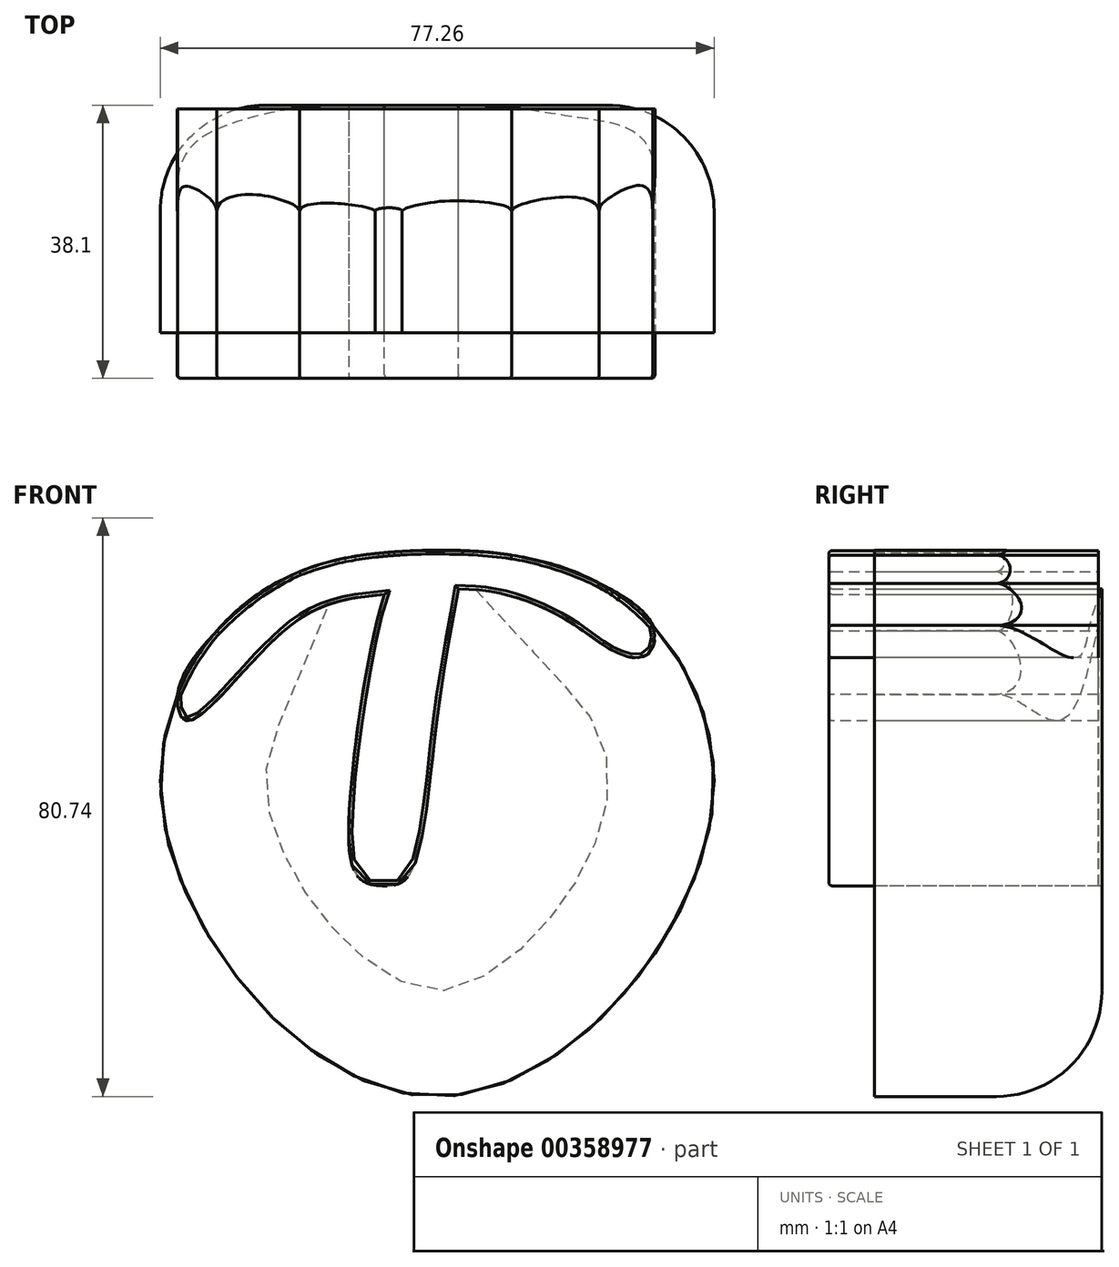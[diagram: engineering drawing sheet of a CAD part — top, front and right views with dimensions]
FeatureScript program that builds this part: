
annotation { "Feature Type Name" : "Feature", "Feature Type Description" : "" }
export const myFeature = defineFeature(function(context is Context, id is Id, definition is map)
    precondition{}
    {
        {
            var Q0;
            Q0=qCreatedBy(makeId("Front.planeOp"),FACE);
            var sketch = newSketch(context, id + "F0", { "sketchPlane" : qUnion([Q0])});
            skFitSpline(sketch, "E0", {"points": [v(0, 38.1) * mm, v(-25.4, 31.75) * mm, v(-38.1, 0) * mm, v(0, -38.1) * mm, v(38.1, 0) * mm, v(25.4, 31.75) * mm, v(0, 38.1) * mm]});
            skFitSpline(sketch, "E1", {"points": [v(-36.21, 18.03) * mm, v(-34.8, 14.34) * mm, v(-20.58, 27.57) * mm, v(-7.35, 31.98) * mm, v(6.86, 32.47) * mm, v(18.62, 28.06) * mm, v(25.49, 23.65) * mm, v(29.4, 23.65) * mm, v(30.05, 27.64) * mm, v(22.58, 33.53) * mm, v(10.37, 37.45) * mm, v(-4.9, 37.98) * mm, v(-19.19, 35.14) * mm, v(-30.73, 26.88) * mm, v(-36.21, 18.03) * mm]});
            skFitSpline(sketch, "E2", {"points": [v(-7.35, 31.98) * mm, v(-12.25, 2.08) * mm, v(-10.78, -7.72) * mm, v(-7.35, -8.7) * mm, v(-3.92, -7.23) * mm, v(0, 14.83) * mm, v(2.95, 32.74) * mm, v(2.45, 34.92) * mm, v(-4.41, 34.92) * mm, v(-7.35, 31.98) * mm]});
            skSolve(sketch);
        }
        {
            var Q0;
            {var subQ0=sQuery(id+"F0.wireOp",EDGE,"E1");var subQ1=sQuery(id+"F0.wireOp",EDGE,"E0");var subQ2=makeQuery(id+"F0.imprint","INTERSECT",VERTEX,{"disambiguationData":[OD(0.0)],"derivedFrom":[subQ1,subQ0]});Q0=makeQuery(id+"F0.imprint","IMPRINT",FACE,{"disambiguationData":[TD([[makeQuery(id+"F0.imprint","IMPRINT",EDGE,{"disambiguationData":[TD([[subQ2,1.0]])],"derivedFrom":subQ1}),1.0]])]});}
            var Q1;
            {var subQ0=sQuery(id+"F0.wireOp",EDGE,"E1");var subQ1=sQuery(id+"F0.wireOp",EDGE,"E0");var subQ2=makeQuery(id+"F0.imprint","INTERSECT",VERTEX,{"disambiguationData":[OD(0.0)],"derivedFrom":[subQ1,subQ0]});Q1=makeQuery(id+"F0.imprint","IMPRINT",FACE,{"disambiguationData":[TD([[makeQuery(id+"F0.imprint","IMPRINT",EDGE,{"disambiguationData":[TD([[subQ2,-1.0]])],"derivedFrom":subQ1}),-1.0]])]});}
            var Q2;
            {var subQ0=sQuery(id+"F0.wireOp",EDGE,"E1");var subQ1=sQuery(id+"F0.wireOp",EDGE,"E0");var subQ2=makeQuery(id+"F0.imprint","INTERSECT",VERTEX,{"disambiguationData":[OD(2.0)],"derivedFrom":[subQ1,subQ0]});Q2=makeQuery(id+"F0.imprint","IMPRINT",FACE,{"disambiguationData":[TD([[makeQuery(id+"F0.imprint","IMPRINT",EDGE,{"disambiguationData":[TD([[subQ2,-1.0]])],"derivedFrom":subQ1}),1.0]])]});}
            var Q3;
            {var subQ0=sQuery(id+"F0.wireOp",EDGE,"E1");var subQ1=sQuery(id+"F0.wireOp",EDGE,"E0");var subQ2=makeQuery(id+"F0.imprint","INTERSECT",VERTEX,{"disambiguationData":[OD(3.0)],"derivedFrom":[subQ1,subQ0]});Q3=makeQuery(id+"F0.imprint","IMPRINT",FACE,{"disambiguationData":[TD([[makeQuery(id+"F0.imprint","IMPRINT",EDGE,{"disambiguationData":[TD([[subQ2,-1.0]])],"derivedFrom":subQ1}),-1.0]])]});}
            var Q4;
            {var subQ0=sQuery(id+"F0.wireOp",EDGE,"E1");var subQ1=sQuery(id+"F0.wireOp",EDGE,"E0");var subQ2=makeQuery(id+"F0.imprint","INTERSECT",VERTEX,{"disambiguationData":[OD(5.0)],"derivedFrom":[subQ1,subQ0]});Q4=makeQuery(id+"F0.imprint","IMPRINT",FACE,{"disambiguationData":[TD([[makeQuery(id+"F0.imprint","IMPRINT",EDGE,{"disambiguationData":[TD([[subQ2,-1.0]])],"derivedFrom":subQ1}),-1.0]])]});}
            var Q5;
            {var subQ0=sQuery(id+"F0.wireOp",EDGE,"E1");var subQ1=sQuery(id+"F0.wireOp",EDGE,"E0");var subQ2=makeQuery(id+"F0.imprint","INTERSECT",VERTEX,{"disambiguationData":[OD(6.0)],"derivedFrom":[subQ1,subQ0]});Q5=makeQuery(id+"F0.imprint","IMPRINT",FACE,{"disambiguationData":[TD([[makeQuery(id+"F0.imprint","IMPRINT",EDGE,{"disambiguationData":[TD([[subQ2,-1.0]])],"derivedFrom":subQ1}),1.0]])]});}
            var Q6;
            {var subQ0=sQuery(id+"F0.wireOp",EDGE,"E1");var subQ1=sQuery(id+"F0.wireOp",EDGE,"E0");var subQ2=makeQuery(id+"F0.imprint","INTERSECT",VERTEX,{"disambiguationData":[OD(1.0)],"derivedFrom":[subQ1,subQ0]});Q6=makeQuery(id+"F0.imprint","IMPRINT",FACE,{"disambiguationData":[TD([[makeQuery(id+"F0.imprint","IMPRINT",EDGE,{"disambiguationData":[TD([[subQ2,1.0]])],"derivedFrom":subQ1}),-1.0]])]});}
            var Q7;
            {var subQ4=sQuery(id+"F0.wireOp",EDGE,"E2");Q7=makeQuery(id+"F0.imprint","IMPRINT",FACE,{"disambiguationData":[TD([[makeQuery(id+"F0.imprint","IMPRINT",EDGE,{"derivedFrom":subQ4}),-1.0]])]});}
            extrude(context, id + "F1", {"entities" : qUnion([Q0, Q1, Q2, Q3, Q4, Q5, Q6, Q7]), "depth" : 31.75 * mm});
        }
        {
            var Q0;
            {var subQ0=sQuery(id+"F0.wireOp",EDGE,"E1");var subQ1=sQuery(id+"F0.wireOp",EDGE,"E0");var subQ9=makeQuery(id+"F0.imprint","INTERSECT",VERTEX,{"disambiguationData":[OD(0.0)],"derivedFrom":[subQ1,subQ0]});Q0=makeQuery(id+"F0.imprint","IMPRINT",FACE,{"disambiguationData":[TD([[makeQuery(id+"F0.imprint","IMPRINT",EDGE,{"disambiguationData":[TD([[subQ9,-1.0]])],"derivedFrom":subQ1}),1.0]])]});}
            var Q1;
            {var subQ0=sQuery(id+"F0.wireOp",EDGE,"E2");Q1=makeQuery(id+"F0.imprint","IMPRINT",FACE,{"disambiguationData":[TD([[makeQuery(id+"F0.imprint","IMPRINT",EDGE,{"derivedFrom":subQ0}),1.0]])]});}
            extrude(context, id + "F2", {"entities" : qUnion([Q0, Q1]), "depth" : 38.1 * mm, "hasSecondDirection" : true, "secondDirectionOppositeDirection" : false, "secondDirectionDepth" : 0.5 * mm});
        }
        {
            var Q0;
            Q0=makeQuery(id+"F2.opExtrude","CAP_FACE",FACE,{"disambiguationData":[OSD([sQuery(id+"F0.wireOp",EDGE,"E0"),sQuery(id+"F0.wireOp",EDGE,"E1"),sQuery(id+"F0.wireOp",EDGE,"E2")])],"isStart":false});
            var Q1;
            Q1=makeQuery(id+"F2.opExtrude","CAP_FACE",FACE,{"disambiguationData":[OSD([sQuery(id+"F0.wireOp",EDGE,"E0"),sQuery(id+"F0.wireOp",EDGE,"E1"),sQuery(id+"F0.wireOp",EDGE,"E2")])],"isStart":false});
            fillet(context, id + "F3", {"entities" : qUnion([Q0, Q1]), "radius" : 0.5 * mm, "tangentPropagation" : true, "allowEdgeOverflow" : false});
        }
        {
            var Q0;
            Q0=makeQuery(id+"F1.opExtrude","CAP_EDGE",EDGE,{"disambiguationData":[OSD([sQuery(id+"F0.wireOp",EDGE,"E0")])],"isStart":true});
            fillet(context, id + "F4", {"entities" : qUnion([Q0]), "radius" : 14.72 * mm, "tangentPropagation" : true, "allowEdgeOverflow" : false});
        }
    });
